# Revit family: HBLHO
name_source: partatom
category: Lighting Fixtures
units: mm (PartAtom-declared; Revit-internal decimal feet)

## family parameters
Cut with Voids When Loaded = No
Host = Face
Light Source = Yes
OmniClass Number = 23.80.70.14.14
OmniClass Title = Exterior Floodlights
Part Type = Normal
Room Calculation Point = No
Round Connector Dimension = Use Diameter
Shared = No

## types (1)
- HBLHO
    Apparent Load = 169 VA
    Application = Convention Center, Gymnasiums, Heavy Industrial
    Certification = UL Sanitation certified per NSF standards,CSA,Wet Listed,Damp Listed,IP Rated,Food Processing (NSF)
    Color Filter = 16777215
    Default Elevation = 48 "
    Description = The HBLHO LED High Bay is designed to efficiently light any large interior space such as heavy industrial settings, warehouses, gyms, churches, swimming pools/natatorium and shopping malls.
    Dimming Lamp Color Temperature Shift = <None>
    Dimming Protocol = 0-10V
    Emit Shape Visible in Rendering = No
    Emit from Circle Diameter = 11 "
    Environmental Conditions = Corrosive, Damp Location, Wet Location
    Fastners = Paint -Light Silver
    Glass = Glass
    IP Rating = IP56
    Lamp = LED
    Load Classification = Lighting
    Manufacturer = Columbia Lighting
    Material Finish = Paint -  White Texture
    Model = HBLHO
    Mounting Type = Pendant, Wall, Ceiling, Stanchion, Cone
    Optics = Narrow
    Photometric Web File = HBLHO72LUA25KN070WH.ies
    Power Factor = 1
    Tilt Angle = -90.00°
    URL = https://www.currentlighting.com
    Voltage = 120 V
    Warranty = 5 Year Warranty
    Watt = 169 W
    Wattage Comments = 169W

## geometry (parser evidence)
native form markers: Blend x4, Sweep x5
no freeform markers — native parametric forms only
